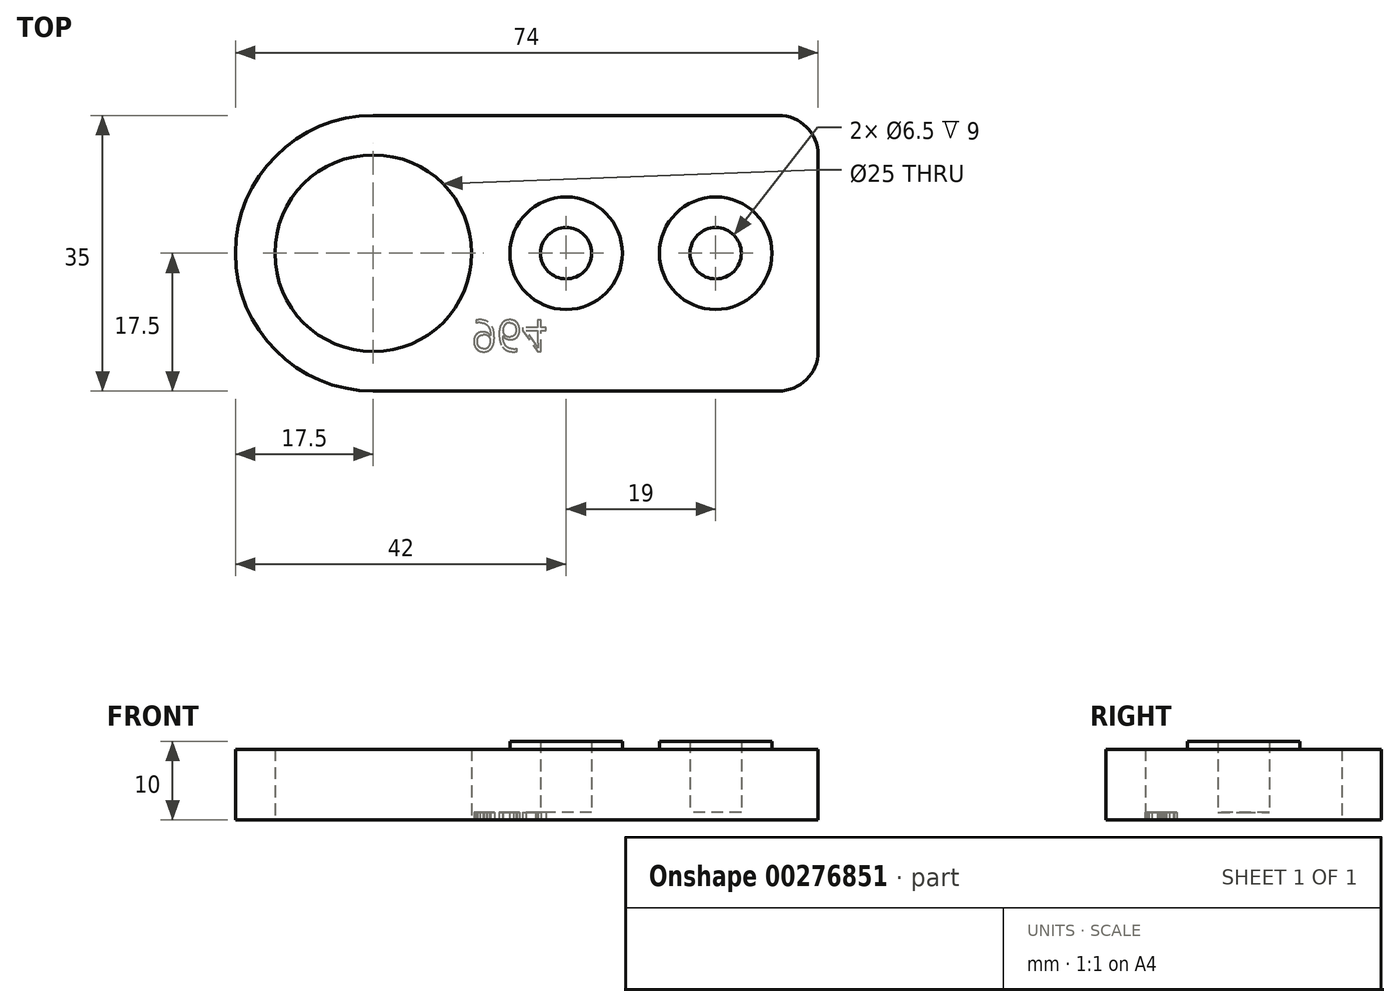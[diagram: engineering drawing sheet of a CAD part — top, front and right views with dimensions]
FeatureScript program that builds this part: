
annotation { "Feature Type Name" : "Feature", "Feature Type Description" : "" }
export const myFeature = defineFeature(function(context is Context, id is Id, definition is map)
    precondition{}
    {
        {
            var Q0;
            Q0=qCreatedBy(makeId("Top.planeOp"),FACE);
            var sketch = newSketch(context, id + "F0", { "sketchPlane" : qUnion([Q0])});
            skLineSegment(sketch, "E0.bottom", {"start": v(17.5, 0) * mm, "end": v(69, 0) * mm});
            skLineSegment(sketch, "E0.top", {"start": v(17.5, 35) * mm, "end": v(69, 35) * mm});
            skLineSegment(sketch, "E0.left", {"start": v(0, 17.5) * mm, "end": v(0, 17.5) * mm});
            skLineSegment(sketch, "E0.right", {"start": v(74, 5) * mm, "end": v(74, 30) * mm});
            skLineSegment(sketch, "E1.bottom", {"start": v(0, 0) * mm, "end": v(17.5, 0) * mm, "construction": true});
            skLineSegment(sketch, "E1.top", {"start": v(0, 17.5) * mm, "end": v(17.5, 17.5) * mm, "construction": true});
            skLineSegment(sketch, "E1.left", {"start": v(0, 0) * mm, "end": v(0, 17.5) * mm, "construction": true});
            skLineSegment(sketch, "E1.right", {"start": v(17.5, 0) * mm, "end": v(17.5, 17.5) * mm, "construction": true});
            skCircle(sketch, "E2", {"center": v(17.5, 17.5) * mm, "radius": 12.5 * mm});
            skPoint(sketch, "E3.visualSharp", {"position": v(0, 0) * mm});
            skArc(sketch, "E3.filletArc", {"start": v(0, 17.5) * mm, "mid": v(5.13, 5.13) * mm, "end": v(17.5, 0) * mm});
            skPoint(sketch, "E4.visualSharp", {"position": v(0, 35) * mm});
            skArc(sketch, "E4.filletArc", {"start": v(17.5, 35) * mm, "mid": v(5.13, 29.87) * mm, "end": v(0, 17.5) * mm});
            skPoint(sketch, "E5.visualSharp", {"position": v(74, 35) * mm});
            skArc(sketch, "E5.filletArc", {"start": v(74, 30) * mm, "mid": v(72.54, 33.54) * mm, "end": v(69, 35) * mm});
            skPoint(sketch, "E6.visualSharp", {"position": v(74, 0) * mm});
            skArc(sketch, "E6.filletArc", {"start": v(69, 0) * mm, "mid": v(72.54, 1.46) * mm, "end": v(74, 5) * mm});
            skSolve(sketch);
        }
        {
            var Q0;
            Q0=makeQuery(id+"F0.imprint","IMPRINT",FACE,{"disambiguationData":[TD([[makeQuery(id+"F0.imprint","IMPRINT",EDGE,{"derivedFrom":sQuery(id+"F0.wireOp",EDGE,"E0.bottom")}),1.0]])]});
            extrude(context, id + "F1", {"entities" : qUnion([Q0]), "depth" : 9 * mm});
        }
        {
            var Q0;
            Q0=makeQuery(id+"F1.opExtrude","CAP_FACE",FACE,{"disambiguationData":[OSD([sQuery(id+"F0.wireOp",EDGE,"E0.bottom"),sQuery(id+"F0.wireOp",EDGE,"E0.top"),sQuery(id+"F0.wireOp",EDGE,"E0.right"),sQuery(id+"F0.wireOp",EDGE,"E2"),sQuery(id+"F0.wireOp",EDGE,"E3.filletArc"),sQuery(id+"F0.wireOp",EDGE,"E4.filletArc"),sQuery(id+"F0.wireOp",EDGE,"E5.filletArc"),sQuery(id+"F0.wireOp",EDGE,"E6.filletArc")])],"isStart":false});
            var sketch = newSketch(context, id + "F2", { "sketchPlane" : qUnion([Q0])});
            skLineSegment(sketch, "E7.bottom", {"start": v(0, 0) * mm, "end": v(42, 0) * mm, "construction": true});
            skLineSegment(sketch, "E7.top", {"start": v(0, 17.5) * mm, "end": v(42, 17.5) * mm, "construction": true});
            skLineSegment(sketch, "E7.left", {"start": v(0, 0) * mm, "end": v(0, 17.5) * mm, "construction": true});
            skLineSegment(sketch, "E7.right", {"start": v(42, 0) * mm, "end": v(42, 17.5) * mm, "construction": true});
            skLineSegment(sketch, "E8", {"start": v(42, 17.5) * mm, "end": v(61, 17.5) * mm, "construction": true});
            skCircle(sketch, "E9", {"center": v(42, 17.5) * mm, "radius": 7.15 * mm});
            skCircle(sketch, "E10", {"center": v(61, 17.5) * mm, "radius": 7.15 * mm});
            skCircle(sketch, "E11", {"center": v(61, 17.5) * mm, "radius": 3.25 * mm});
            skCircle(sketch, "E12", {"center": v(42, 17.5) * mm, "radius": 3.25 * mm});
            skSolve(sketch);
        }
        {
            var Q0;
            Q0=makeQuery(id+"F2.imprint","IMPRINT",FACE,{"disambiguationData":[TD([[makeQuery(id+"F2.imprint","IMPRINT",EDGE,{"derivedFrom":sQuery(id+"F2.wireOp",EDGE,"E9")}),1.0]])]});
            var Q1;
            Q1=makeQuery(id+"F2.imprint","IMPRINT",FACE,{"disambiguationData":[TD([[makeQuery(id+"F2.imprint","IMPRINT",EDGE,{"derivedFrom":sQuery(id+"F2.wireOp",EDGE,"E10")}),1.0]])]});
            extrude(context, id + "F3", {"entities" : qUnion([Q0, Q1]), "operationType" : NewBodyOperationType.ADD, "depth" : 1 * mm});
        }
        {
            var Q0;
            Q0=makeQuery(id+"F3.boolean.opBoolean","SPLIT",FACE,{"disambiguationData":[TD([makeQuery(id+"F3.opExtrude","SWEPT_FACE",FACE,{"disambiguationData":[OSD([sQuery(id+"F2.wireOp",EDGE,"E12")])]})])],"derivedFrom":makeQuery(id+"F1.opExtrude","CAP_FACE",FACE,{"disambiguationData":[OSD([sQuery(id+"F0.wireOp",EDGE,"E0.bottom"),sQuery(id+"F0.wireOp",EDGE,"E0.top"),sQuery(id+"F0.wireOp",EDGE,"E0.right"),sQuery(id+"F0.wireOp",EDGE,"E2"),sQuery(id+"F0.wireOp",EDGE,"E3.filletArc"),sQuery(id+"F0.wireOp",EDGE,"E4.filletArc"),sQuery(id+"F0.wireOp",EDGE,"E5.filletArc"),sQuery(id+"F0.wireOp",EDGE,"E6.filletArc")])],"isStart":false})});
            var Q1;
            Q1=makeQuery(id+"F3.boolean.opBoolean","SPLIT",FACE,{"disambiguationData":[TD([makeQuery(id+"F3.opExtrude","SWEPT_FACE",FACE,{"disambiguationData":[OSD([sQuery(id+"F2.wireOp",EDGE,"E11")])]})])],"derivedFrom":makeQuery(id+"F1.opExtrude","CAP_FACE",FACE,{"disambiguationData":[OSD([sQuery(id+"F0.wireOp",EDGE,"E0.bottom"),sQuery(id+"F0.wireOp",EDGE,"E0.top"),sQuery(id+"F0.wireOp",EDGE,"E0.right"),sQuery(id+"F0.wireOp",EDGE,"E2"),sQuery(id+"F0.wireOp",EDGE,"E3.filletArc"),sQuery(id+"F0.wireOp",EDGE,"E4.filletArc"),sQuery(id+"F0.wireOp",EDGE,"E5.filletArc"),sQuery(id+"F0.wireOp",EDGE,"E6.filletArc")])],"isStart":false})});
            extrude(context, id + "F4", {"entities" : qUnion([Q0, Q1]), "operationType" : NewBodyOperationType.REMOVE, "oppositeDirection" : true, "depth" : 8 * mm});
        }
        {
            var Q0;
            Q0=makeQuery(id+"F1.opExtrude","CAP_FACE",FACE,{"disambiguationData":[OSD([sQuery(id+"F0.wireOp",EDGE,"E0.bottom"),sQuery(id+"F0.wireOp",EDGE,"E0.top"),sQuery(id+"F0.wireOp",EDGE,"E0.right"),sQuery(id+"F0.wireOp",EDGE,"E2"),sQuery(id+"F0.wireOp",EDGE,"E3.filletArc"),sQuery(id+"F0.wireOp",EDGE,"E4.filletArc"),sQuery(id+"F0.wireOp",EDGE,"E5.filletArc"),sQuery(id+"F0.wireOp",EDGE,"E6.filletArc")])],"isStart":true});
            var sketch = newSketch(context, id + "F5", { "sketchPlane" : qUnion([Q0])});
            skLineSegment(sketch, "E13.bottom", {"start": v(0, 0) * mm, "end": v(30, 0) * mm, "construction": true});
            skLineSegment(sketch, "E13.top", {"start": v(0, -5) * mm, "end": v(30, -5) * mm, "construction": true});
            skLineSegment(sketch, "E13.left", {"start": v(0, 0) * mm, "end": v(0, -5) * mm, "construction": true});
            skLineSegment(sketch, "E13.right", {"start": v(30, 0) * mm, "end": v(30, -5) * mm, "construction": true});
            skText(sketch, "E14", { "text": "964", "fontName": "OpenSans-Regular.ttf"});
            const initialGuessF5  = {"E14": [0.03, -0.009, 1, 0, 0.004]};
            skSetInitialGuess(sketch, initialGuessF5);
            skSolve(sketch);
        }
        {
            var Q0;
            Q0 = qSketchRegion(id + "F5", true);
            extrude(context, id + "F6", {"entities" : qUnion([Q0]), "operationType" : NewBodyOperationType.REMOVE, "oppositeDirection" : true, "depth" : 1 * mm});
        }
    });
